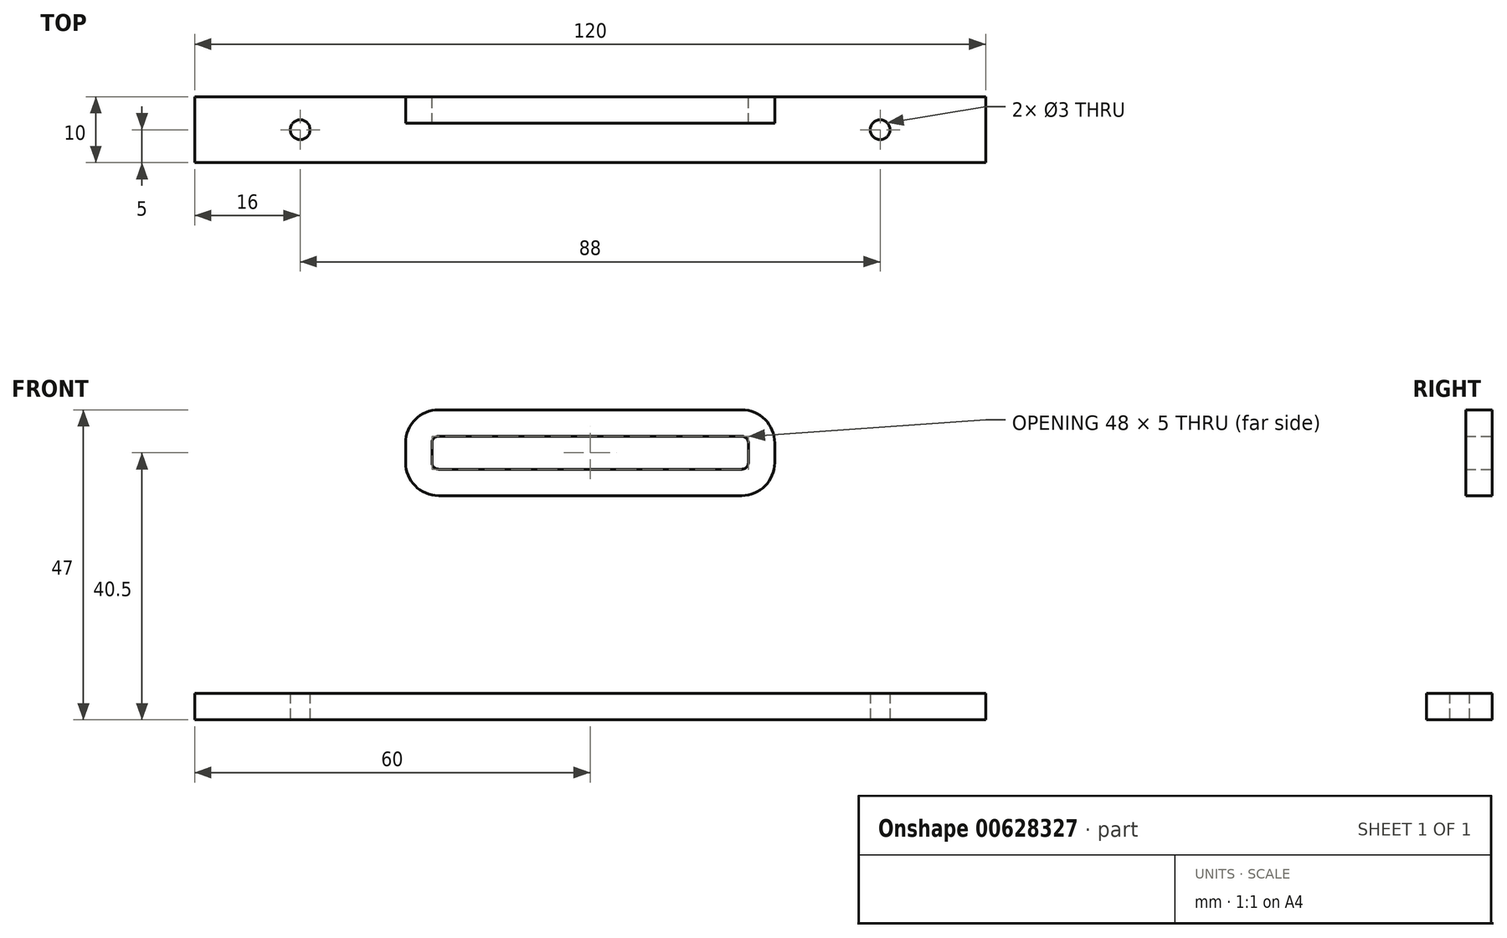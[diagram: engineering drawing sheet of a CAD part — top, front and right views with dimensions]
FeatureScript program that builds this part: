
annotation { "Feature Type Name" : "Feature", "Feature Type Description" : "" }
export const myFeature = defineFeature(function(context is Context, id is Id, definition is map)
    precondition{}
    {
        {
            var Q0;
            Q0=qCreatedBy(makeId("Top.planeOp"),FACE);
            var sketch = newSketch(context, id + "F0", { "sketchPlane" : qUnion([Q0])});
            skLineSegment(sketch, "E0.bottom", {"start": v(0, 0) * mm, "end": v(120, 0) * mm});
            skLineSegment(sketch, "E0.top", {"start": v(0, 10) * mm, "end": v(120, 10) * mm});
            skLineSegment(sketch, "E0.left", {"start": v(0, 0) * mm, "end": v(0, 10) * mm});
            skLineSegment(sketch, "E0.right", {"start": v(120, 0) * mm, "end": v(120, 10) * mm});
            skLineSegment(sketch, "E1", {"start": v(0, 5) * mm, "end": v(120, 5) * mm, "construction": true});
            skCircle(sketch, "E2", {"center": v(16, 5) * mm, "radius": 1.5 * mm});
            skLineSegment(sketch, "E3", {"start": v(60, 10) * mm, "end": v(60, 0) * mm, "construction": true});
            skCircle(sketch, "E4.MirrorC", {"center": v(104, 5) * mm, "radius": 1.5 * mm});
            skSolve(sketch);
        }
        {
            var Q0;
            Q0=makeQuery(id+"F0.imprint","IMPRINT",FACE,{"disambiguationData":[TD([[makeQuery(id+"F0.imprint","IMPRINT",EDGE,{"derivedFrom":sQuery(id+"F0.wireOp",EDGE,"E0.bottom")}),1.0]])]});
            extrude(context, id + "F1", {"entities" : qUnion([Q0]), "endBound" : BoundingType.SYMMETRIC, "depth" : 4 * mm, "offsetDistance" : 25 * mm});
        }
        {
            var Q0;
            Q0=makeQuery(id+"F1.opExtrude","SWEPT_FACE",FACE,{"disambiguationData":[OSD([sQuery(id+"F0.wireOp",EDGE,"E0.top")])]});
            var sketch = newSketch(context, id + "F2", { "sketchPlane" : qUnion([Q0])});
            skLineSegment(sketch, "E5.0", {"start": v(0, 2) * mm, "end": v(-120, 2) * mm});
            skLineSegment(sketch, "E6", {"start": v(-60, 2) * mm, "end": v(-60, 26.3) * mm, "construction": true});
            skPoint(sketch, "E6.endSnap0", {"position": v(-60, 2) * mm});
            skLineSegment(sketch, "E7.bottom", {"start": v(-63, 2) * mm, "end": v(-57, 2) * mm});
            skLineSegment(sketch, "E7.top", {"start": v(-63, 32) * mm, "end": v(-57, 32) * mm});
            skLineSegment(sketch, "E7.left", {"start": v(-63, 2) * mm, "end": v(-63, 32) * mm});
            skLineSegment(sketch, "E7.right", {"start": v(-57, 2) * mm, "end": v(-57, 32) * mm});
            skLineSegment(sketch, "E8.bottom", {"start": v(-83, 32) * mm, "end": v(-37, 32) * mm});
            skLineSegment(sketch, "E8.top", {"start": v(-83, 45) * mm, "end": v(-37, 45) * mm});
            skLineSegment(sketch, "E8.left", {"start": v(-88, 37) * mm, "end": v(-88, 40) * mm});
            skLineSegment(sketch, "E8.right", {"start": v(-32, 37) * mm, "end": v(-32, 40) * mm});
            skPoint(sketch, "E9.visualSharp", {"position": v(-88, 45) * mm});
            skArc(sketch, "E9.filletArc", {"start": v(-83, 45) * mm, "mid": v(-86.54, 43.54) * mm, "end": v(-88, 40) * mm});
            skPoint(sketch, "E10.visualSharp", {"position": v(-88, 32) * mm});
            skArc(sketch, "E10.filletArc", {"start": v(-88, 37) * mm, "mid": v(-86.54, 33.46) * mm, "end": v(-83, 32) * mm});
            skPoint(sketch, "E11.visualSharp", {"position": v(-32, 45) * mm});
            skArc(sketch, "E11.filletArc", {"start": v(-32, 40) * mm, "mid": v(-33.46, 43.54) * mm, "end": v(-37, 45) * mm});
            skPoint(sketch, "E12.visualSharp", {"position": v(-32, 32) * mm});
            skArc(sketch, "E12.filletArc", {"start": v(-37, 32) * mm, "mid": v(-33.46, 33.46) * mm, "end": v(-32, 37) * mm});
            skArc(sketch, "E13.0", {"start": v(-83, 41) * mm, "mid": v(-83.7, 40.7) * mm, "end": v(-84, 40) * mm});
            skLineSegment(sketch, "E13.1", {"start": v(-84, 37) * mm, "end": v(-84, 40) * mm});
            skLineSegment(sketch, "E13.2", {"start": v(-83, 41) * mm, "end": v(-37, 41) * mm});
            skArc(sketch, "E13.3", {"start": v(-84, 37) * mm, "mid": v(-83.7, 36.3) * mm, "end": v(-83, 36) * mm});
            skArc(sketch, "E13.4", {"start": v(-36, 40) * mm, "mid": v(-36.3, 40.7) * mm, "end": v(-37, 41) * mm});
            skLineSegment(sketch, "E13.5", {"start": v(-36, 37) * mm, "end": v(-36, 40) * mm});
            skArc(sketch, "E13.6", {"start": v(-37, 36) * mm, "mid": v(-36.3, 36.3) * mm, "end": v(-36, 37) * mm});
            skLineSegment(sketch, "E13.7", {"start": v(-83, 36) * mm, "end": v(-37, 36) * mm});
            skSolve(sketch);
        }
        {
            var Q0;
            Q0=makeQuery(id+"F2.imprint","IMPRINT",FACE,{"disambiguationData":[TD([[makeQuery(id+"F2.imprint","IMPRINT",EDGE,{"derivedFrom":sQuery(id+"F2.wireOp",EDGE,"E8.top")}),-1.0]])]});
            var Q1;
            Q1=makeQuery(id+"F2.imprint","IMPRINT",FACE,{"disambiguationData":[TD([[makeQuery(id+"F2.imprint","IMPRINT",EDGE,{"derivedFrom":sQuery(id+"F2.wireOp",EDGE,"E7.bottom")}),-1.0]])]});
            extrude(context, id + "F3", {"entities" : qUnion([Q0, Q1]), "operationType" : NewBodyOperationType.ADD, "oppositeDirection" : true, "depth" : 4 * mm, "offsetDistance" : 25 * mm});
        }
    });
